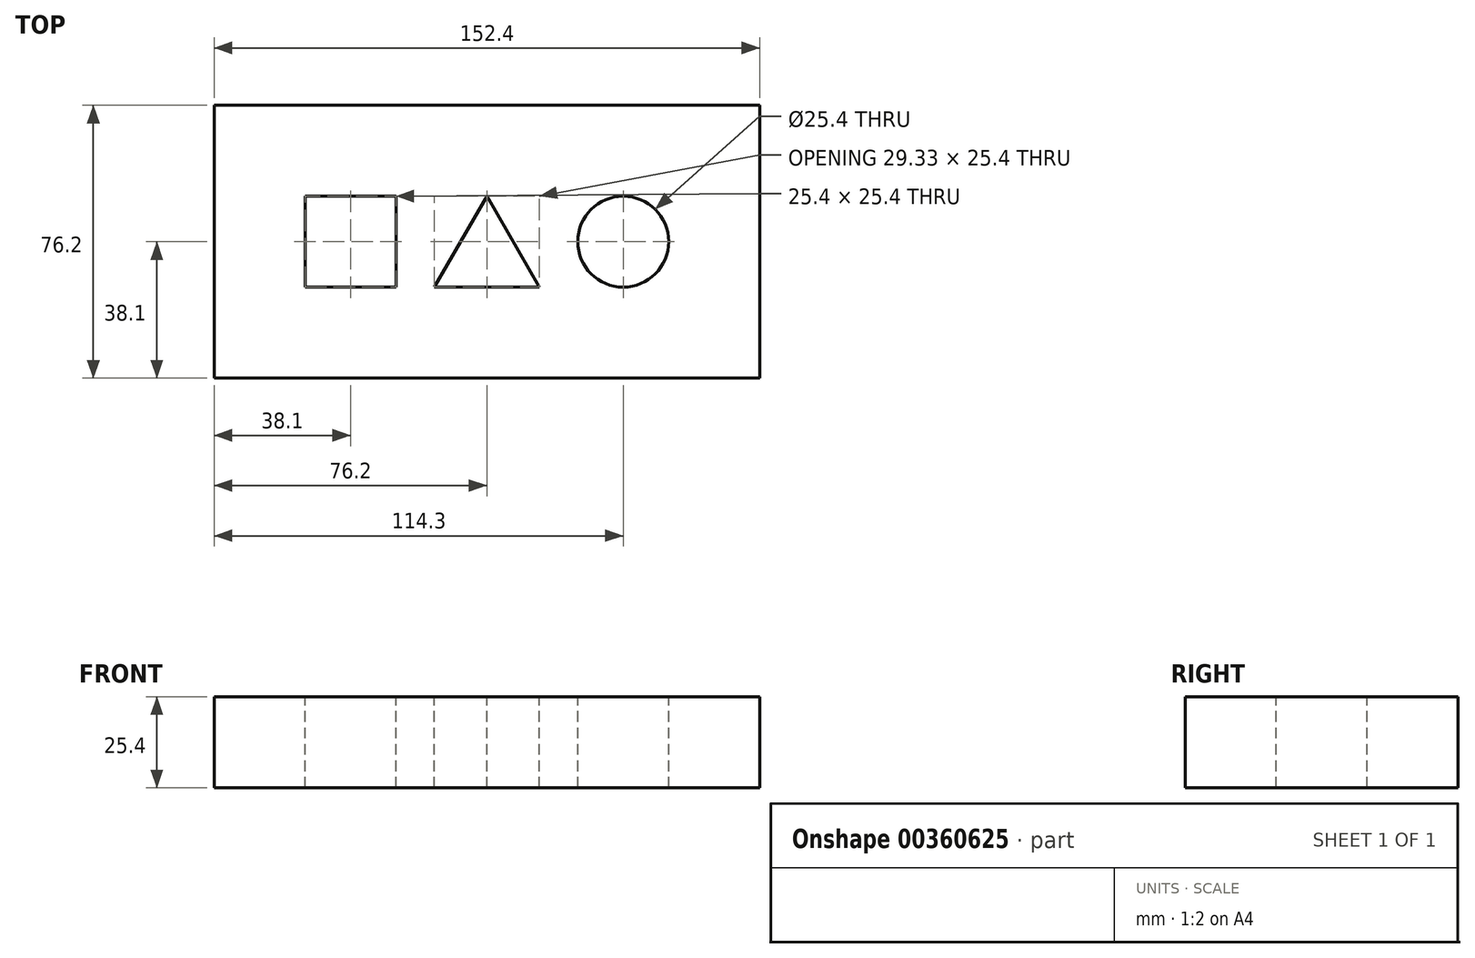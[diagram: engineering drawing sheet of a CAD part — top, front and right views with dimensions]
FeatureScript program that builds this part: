
annotation { "Feature Type Name" : "Feature", "Feature Type Description" : "" }
export const myFeature = defineFeature(function(context is Context, id is Id, definition is map)
    precondition{}
    {
        {
            var Q0;
            Q0=qCreatedBy(makeId("Front.planeOp"),FACE);
            var sketch = newSketch(context, id + "F0", { "sketchPlane" : qUnion([Q0])});
            skLineSegment(sketch, "E0.bottom", {"start": v(0, 0) * mm, "end": v(152.4, 0) * mm});
            skLineSegment(sketch, "E0.top", {"start": v(0, -25.4) * mm, "end": v(152.4, -25.4) * mm});
            skLineSegment(sketch, "E0.left", {"start": v(0, 0) * mm, "end": v(0, -25.4) * mm});
            skLineSegment(sketch, "E0.right", {"start": v(152.4, 0) * mm, "end": v(152.4, -25.4) * mm});
            skSolve(sketch);
        }
        {
            var Q0;
            Q0=makeQuery(id+"F0.imprint","IMPRINT",FACE,{"disambiguationData":[TD([[makeQuery(id+"F0.imprint","IMPRINT",EDGE,{"derivedFrom":sQuery(id+"F0.wireOp",EDGE,"E0.bottom")}),-1.0]])]});
            extrude(context, id + "F1", {"entities" : qUnion([Q0]), "depth" : 76.2 * mm});
        }
        {
            var Q0;
            Q0=makeQuery(id+"F1.opExtrude","SWEPT_FACE",FACE,{"disambiguationData":[OSD([sQuery(id+"F0.wireOp",EDGE,"E0.bottom")])]});
            var sketch = newSketch(context, id + "F2", { "sketchPlane" : qUnion([Q0])});
            skLineSegment(sketch, "E1.bottom", {"start": v(50.8, -25.4) * mm, "end": v(25.4, -25.4) * mm});
            skLineSegment(sketch, "E1.top", {"start": v(50.8, -50.8) * mm, "end": v(25.4, -50.8) * mm});
            skLineSegment(sketch, "E1.left", {"start": v(50.8, -25.4) * mm, "end": v(50.8, -50.8) * mm});
            skLineSegment(sketch, "E1.right", {"start": v(25.4, -25.4) * mm, "end": v(25.4, -50.8) * mm});
            skPoint(sketch, "E1.middle", {"position": v(38.1, -38.1) * mm});
            skCircle(sketch, "E2", {"center": v(114.3, -38.1) * mm, "radius": 12.7 * mm});
            skLineSegment(sketch, "E3", {"start": v(61.54, -50.8) * mm, "end": v(90.86, -50.8) * mm});
            skLineSegment(sketch, "E4", {"start": v(90.86, -50.8) * mm, "end": v(76.2, -25.4) * mm});
            skLineSegment(sketch, "E5", {"start": v(76.2, -25.4) * mm, "end": v(61.54, -50.8) * mm});
            skLineSegment(sketch, "E6", {"start": v(76.2, -25.4) * mm, "end": v(76.2, -50.8) * mm});
            skLineSegment(sketch, "E7", {"start": v(76.2, -50.8) * mm, "end": v(76.2, -38.1) * mm});
            skSolve(sketch);
        }
        {
            var Q0;
            Q0=makeQuery(id+"F2.imprint","IMPRINT",FACE,{"disambiguationData":[TD([[makeQuery(id+"F2.imprint","IMPRINT",EDGE,{"derivedFrom":sQuery(id+"F2.wireOp",EDGE,"E1.bottom")}),1.0]])]});
            var Q1;
            {var subQ0=sQuery(id+"F2.wireOp",EDGE,"E5");Q1=makeQuery(id+"F2.imprint","IMPRINT",FACE,{"disambiguationData":[TD([[makeQuery(id+"F2.imprint","IMPRINT",EDGE,{"derivedFrom":subQ0}),1.0]])]});}
            var Q2;
            {var subQ0=sQuery(id+"F2.wireOp",EDGE,"E4");Q2=makeQuery(id+"F2.imprint","IMPRINT",FACE,{"disambiguationData":[TD([[makeQuery(id+"F2.imprint","IMPRINT",EDGE,{"derivedFrom":subQ0}),1.0]])]});}
            var Q3;
            Q3=makeQuery(id+"F2.imprint","IMPRINT",FACE,{"disambiguationData":[TD([[makeQuery(id+"F2.imprint","IMPRINT",EDGE,{"derivedFrom":sQuery(id+"F2.wireOp",EDGE,"E2")}),1.0]])]});
            extrude(context, id + "F3", {"entities" : qUnion([Q0, Q1, Q2, Q3]), "operationType" : NewBodyOperationType.REMOVE, "oppositeDirection" : true, "depth" : 25.4 * mm});
        }
    });
